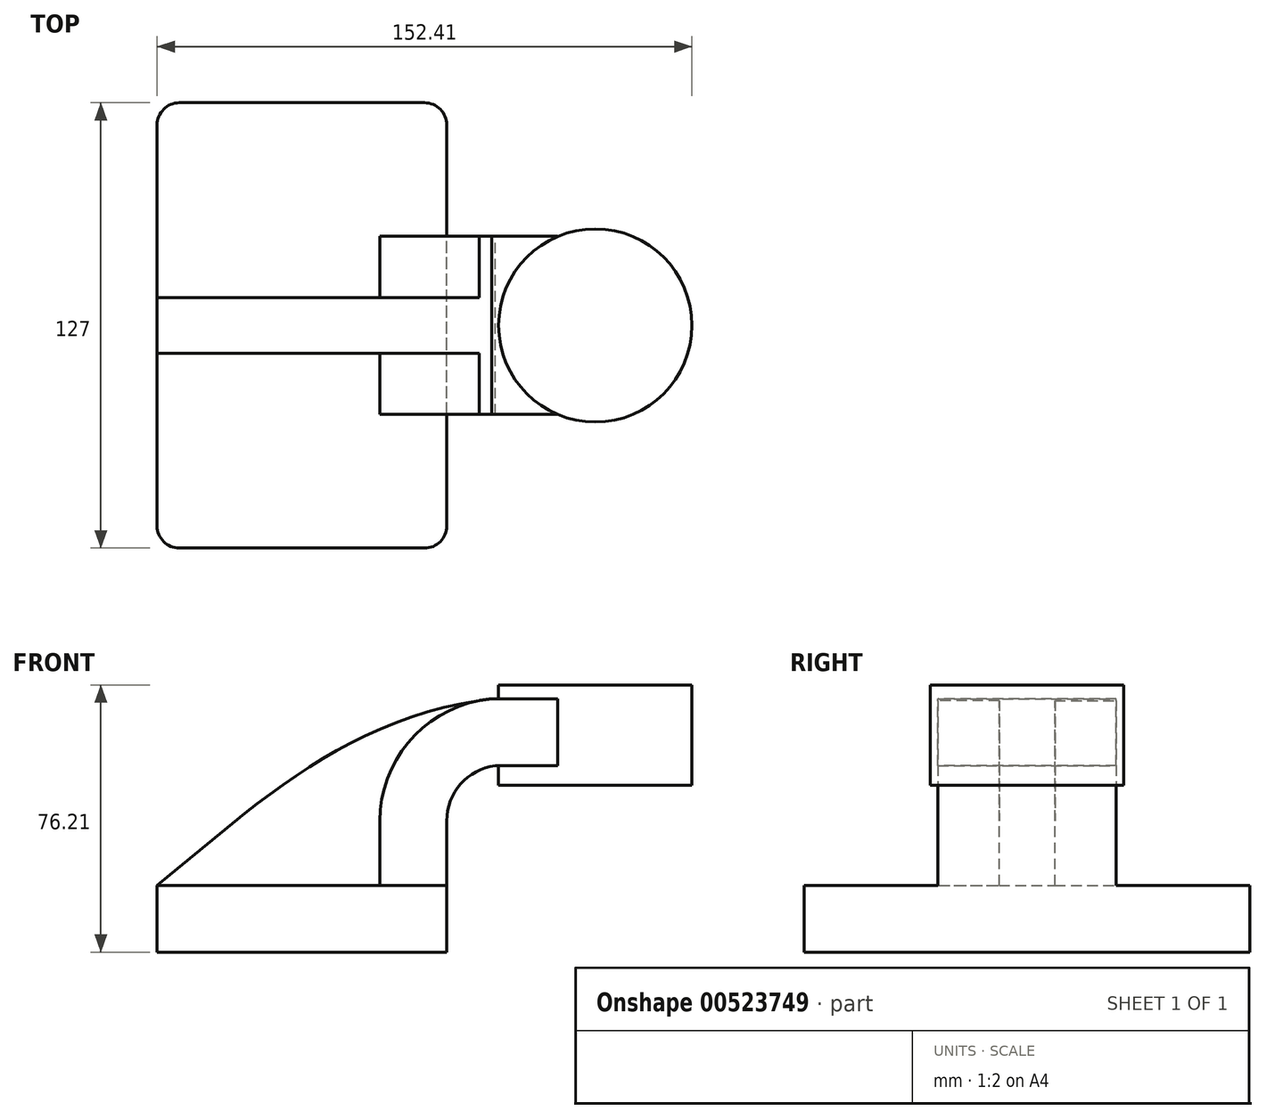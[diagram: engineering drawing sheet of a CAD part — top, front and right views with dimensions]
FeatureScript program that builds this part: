
annotation { "Feature Type Name" : "Feature", "Feature Type Description" : "" }
export const myFeature = defineFeature(function(context is Context, id is Id, definition is map)
    precondition{}
    {
        {
            var Q0;
            Q0=qCreatedBy(makeId("Front.planeOp"),FACE);
            var sketch = newSketch(context, id + "F0", { "sketchPlane" : qUnion([Q0])});
            skLineSegment(sketch, "E0.bottom", {"start": v(41.27, 9.53) * mm, "end": v(-41.28, 9.53) * mm});
            skLineSegment(sketch, "E0.top", {"start": v(41.28, -9.52) * mm, "end": v(-41.27, -9.52) * mm});
            skLineSegment(sketch, "E0.left", {"start": v(41.28, 9.53) * mm, "end": v(41.28, -9.52) * mm});
            skLineSegment(sketch, "E0.right", {"start": v(-41.28, 9.53) * mm, "end": v(-41.27, -9.52) * mm});
            skPoint(sketch, "E0.middle", {"position": v(0, 0) * mm});
            skLineSegment(sketch, "E1.bottom", {"start": v(111.12, 38.1) * mm, "end": v(60.32, 38.1) * mm});
            skLineSegment(sketch, "E1.top", {"start": v(111.12, 66.68) * mm, "end": v(60.32, 66.68) * mm});
            skLineSegment(sketch, "E1.left", {"start": v(111.12, 38.1) * mm, "end": v(111.12, 66.68) * mm});
            skLineSegment(sketch, "E1.right", {"start": v(60.32, 38.1) * mm, "end": v(60.32, 66.67) * mm});
            skPoint(sketch, "E1.middle", {"position": v(85.72, 52.39) * mm});
            skLineSegment(sketch, "E2", {"start": v(41.27, 9.53) * mm, "end": v(41.27, 27.92) * mm});
            skArc(sketch, "E3", {"start": v(41.27, 27.92) * mm, "mid": v(45.21, 38.38) * mm, "end": v(55.07, 43.65) * mm});
            skLineSegment(sketch, "E4", {"start": v(55.07, 43.65) * mm, "end": v(83.57, 43.65) * mm});
            skLineSegment(sketch, "E5.0", {"start": v(54.06, 62.7) * mm, "end": v(83.57, 62.7) * mm});
            skArc(sketch, "E5.1", {"start": v(22.23, 27.92) * mm, "mid": v(31.38, 51.5) * mm, "end": v(54.06, 62.7) * mm});
            skLineSegment(sketch, "E5.2", {"start": v(22.22, 9.53) * mm, "end": v(22.22, 27.92) * mm});
            skLineSegment(sketch, "E6", {"start": v(83.57, 62.7) * mm, "end": v(83.57, 43.65) * mm});
            skFitSpline(sketch, "E7", {"points": [v(-41.28, 9.52) * mm, v(54.06, 62.7) * mm], "startDerivative": vector(86.4, 69.74) * mm, "endDerivative": vector(125.9, 15.8) * mm});
            skLineSegment(sketch, "E8", {"start": v(83.57, 62.7) * mm, "end": v(83.57, 66.68) * mm});
            skLineSegment(sketch, "E9", {"start": v(83.57, 43.65) * mm, "end": v(83.57, 38.1) * mm});
            skSolve(sketch);
        }
        {
            var Q0;
            Q0=makeQuery(id+"F0.imprint","IMPRINT",FACE,{"disambiguationData":[TD([[makeQuery(id+"F0.imprint","IMPRINT",EDGE,{"derivedFrom":sQuery(id+"F0.wireOp",EDGE,"E0.top")}),-1.0]])]});
            extrude(context, id + "F1", {"entities" : qUnion([Q0]), "endBound" : BoundingType.SYMMETRIC, "depth" : 127 * mm, "offsetDistance" : 25.4 * mm});
        }
        {
            var Q0;
            {var subQ1=sQuery(id+"F0.wireOp",EDGE,"E2");Q0=makeQuery(id+"F0.imprint","IMPRINT",FACE,{"disambiguationData":[TD([[makeQuery(id+"F0.imprint","IMPRINT",EDGE,{"derivedFrom":subQ1}),1.0]])]});}
            extrude(context, id + "F2", {"entities" : qUnion([Q0]), "operationType" : NewBodyOperationType.ADD, "endBound" : BoundingType.SYMMETRIC, "depth" : 50.8 * mm, "offsetDistance" : 25.4 * mm});
        }
        {
            var Q0;
            {var subQ3=sQuery(id+"F0.wireOp",EDGE,"E5.2");Q0=makeQuery(id+"F0.imprint","IMPRINT",FACE,{"disambiguationData":[TD([[makeQuery(id+"F0.imprint","IMPRINT",EDGE,{"derivedFrom":subQ3}),1.0]])]});}
            extrude(context, id + "F3", {"entities" : qUnion([Q0]), "operationType" : NewBodyOperationType.ADD, "endBound" : BoundingType.SYMMETRIC, "depth" : 15.88 * mm, "offsetDistance" : 25.4 * mm});
        }
        {
            var Q0;
            Q0=makeQuery(id+"F2.opExtrude","SWEPT_FACE",FACE,{"disambiguationData":[OSD([sQuery(id+"F0.wireOp",EDGE,"E1.right")])]});
            extrude(context, id + "F4", {"entities" : qUnion([Q0]), "operationType" : NewBodyOperationType.ADD, "depth" : 12.7 * mm, "offsetDistance" : 25.4 * mm});
        }
        {
            var Q0;
            {var subQ0=sQuery(id+"F0.wireOp",EDGE,"E1.left");Q0=makeQuery(id+"F0.imprint","IMPRINT",FACE,{"disambiguationData":[TD([[makeQuery(id+"F0.imprint","IMPRINT",EDGE,{"derivedFrom":subQ0}),1.0]])]});}
            var Q1;
            Q1=sQuery(id+"F0.wireOp",EDGE,"E9");
            revolve(context, id + "F5", {"operationType" : NewBodyOperationType.ADD, "entities" : qUnion([Q0]), "axis" : qUnion([Q1]), "revolveType" : RevolveType.FULL});
        }
        {
            var Q0;
            Q0=makeQuery(id+"F1.opExtrude","CAP_EDGE",EDGE,{"disambiguationData":[OSD([sQuery(id+"F0.wireOp",EDGE,"E0.right")])],"isStart":false});
            var Q1;
            Q1=makeQuery(id+"F1.opExtrude","CAP_EDGE",EDGE,{"disambiguationData":[OSD([sQuery(id+"F0.wireOp",EDGE,"E0.left")])],"isStart":false});
            var Q2;
            Q2=makeQuery(id+"F1.opExtrude","CAP_EDGE",EDGE,{"disambiguationData":[OSD([sQuery(id+"F0.wireOp",EDGE,"E0.left")])],"isStart":true});
            var Q3;
            Q3=makeQuery(id+"F1.opExtrude","CAP_EDGE",EDGE,{"disambiguationData":[OSD([sQuery(id+"F0.wireOp",EDGE,"E0.right")])],"isStart":true});
            fillet(context, id + "F6", {"entities" : qUnion([Q0, Q1, Q2, Q3]), "radius" : 6.35 * mm, "tangentPropagation" : true, "allowEdgeOverflow" : false});
        }
    });
